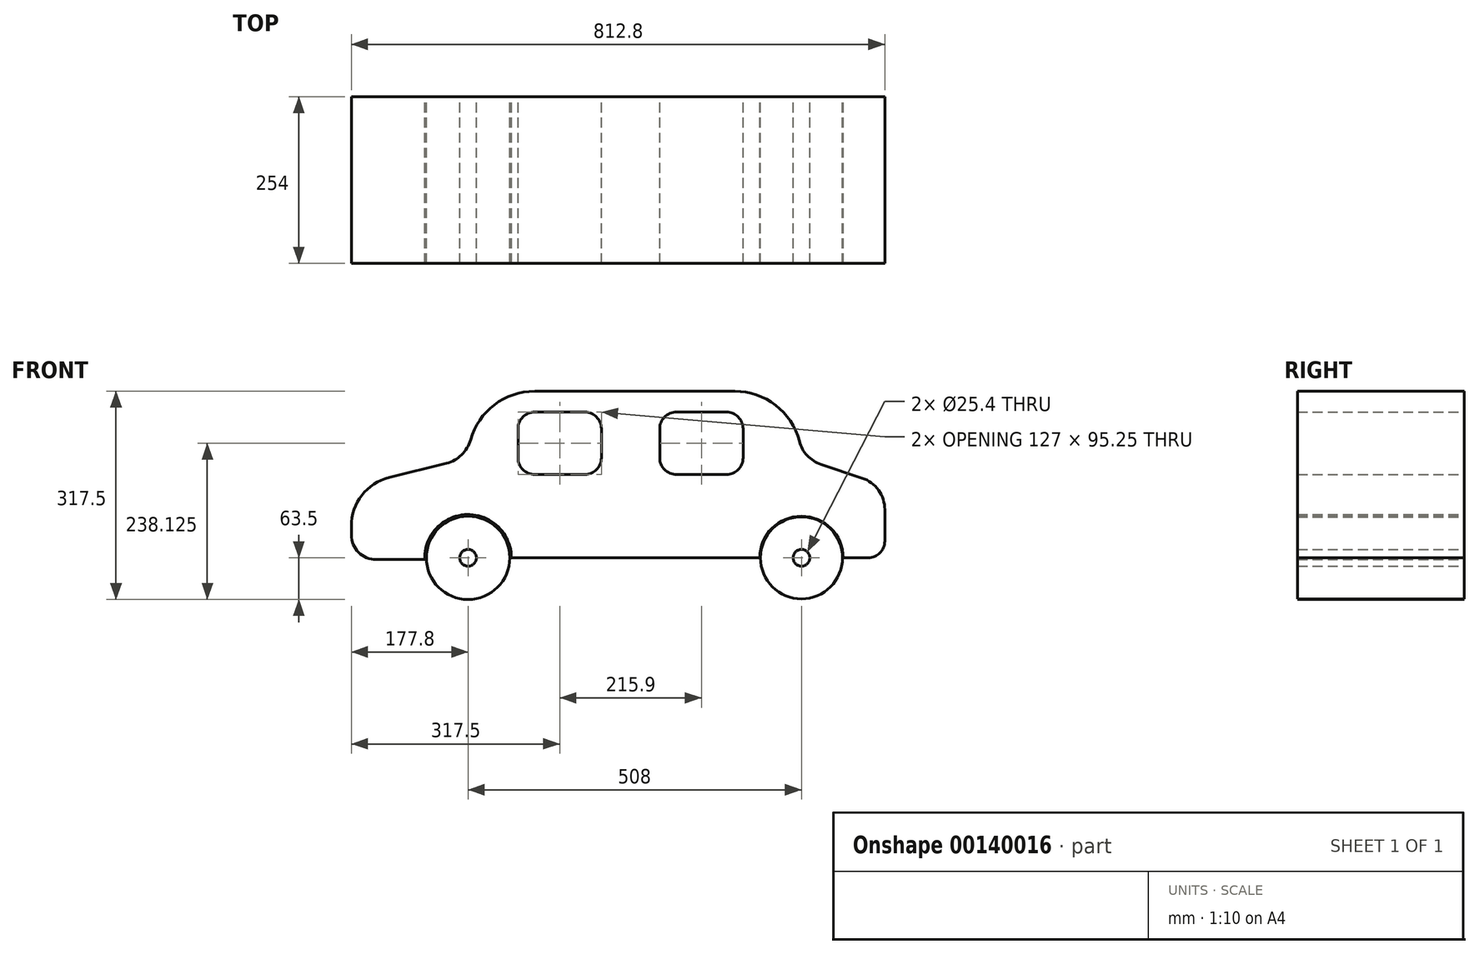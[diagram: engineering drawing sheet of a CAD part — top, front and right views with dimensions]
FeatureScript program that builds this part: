
annotation { "Feature Type Name" : "Feature", "Feature Type Description" : "" }
export const myFeature = defineFeature(function(context is Context, id is Id, definition is map)
    precondition{}
    {
        {
            var Q0;
            Q0=qCreatedBy(makeId("Front.planeOp"),FACE);
            var sketch = newSketch(context, id + "F0", { "sketchPlane" : qUnion([Q0])});
            skLineSegment(sketch, "E0.bottom", {"start": v(-152.4, 127) * mm, "end": v(152.4, 127) * mm});
            skLineSegment(sketch, "E0.left", {"start": v(-254, 25.4) * mm, "end": v(-254, 25.4) * mm});
            skLineSegment(sketch, "E0.right", {"start": v(254, 25.4) * mm, "end": v(254, 25.4) * mm});
            skPoint(sketch, "E0.middle", {"position": v(0, 0) * mm});
            skLineSegment(sketch, "E1.top", {"start": v(316.52, -127) * mm, "end": v(355.6, -127) * mm});
            skLineSegment(sketch, "E1.left", {"start": v(254, -127) * mm, "end": v(254, -127) * mm});
            skLineSegment(sketch, "E1.right", {"start": v(381, -53.55) * mm, "end": v(381, -101.6) * mm});
            skLineSegment(sketch, "E2.top", {"start": v(-319.98, -129.78) * mm, "end": v(-393.7, -129.78) * mm});
            skLineSegment(sketch, "E2.left", {"start": v(-254, -127) * mm, "end": v(-254, -129.78) * mm});
            skLineSegment(sketch, "E2.right", {"start": v(-431.8, -78.55) * mm, "end": v(-431.8, -91.68) * mm});
            skPoint(sketch, "E3.visualSharp", {"position": v(-254, 127) * mm});
            skPoint(sketch, "E4.visualSharp", {"position": v(254, 127) * mm});
            skArc(sketch, "E4.filletArc", {"start": v(250.75, 50.9) * mm, "mid": v(214.58, 105.75) * mm, "end": v(152.4, 127) * mm});
            skPoint(sketch, "E5.visualSharp", {"position": v(254, 25.4) * mm});
            skPoint(sketch, "E6.visualSharp", {"position": v(254, 0) * mm});
            skPoint(sketch, "E7.visualSharp", {"position": v(381, 0) * mm});
            skArc(sketch, "E7.filletArc", {"start": v(381, -53.55) * mm, "mid": v(371.41, -23.84) * mm, "end": v(346.26, -5.35) * mm});
            skPoint(sketch, "E8.visualSharp", {"position": v(-254, 0) * mm});
            skPoint(sketch, "E9.visualSharp", {"position": v(-431.8, 0) * mm});
            skArc(sketch, "E9.filletArc", {"start": v(-374.08, -4.62) * mm, "mid": v(-415.66, -31.65) * mm, "end": v(-431.8, -78.55) * mm});
            skPoint(sketch, "E10.visualSharp", {"position": v(-431.8, -129.78) * mm});
            skArc(sketch, "E10.filletArc", {"start": v(-431.8, -91.68) * mm, "mid": v(-420.64, -118.62) * mm, "end": v(-393.7, -129.78) * mm});
            skPoint(sketch, "E11.visualSharp", {"position": v(381, -127) * mm});
            skArc(sketch, "E11.filletArc", {"start": v(355.6, -127) * mm, "mid": v(373.56, -119.56) * mm, "end": v(381, -101.6) * mm});
            skLineSegment(sketch, "E12.bottom", {"start": v(-152.4, 95.25) * mm, "end": v(-76.2, 95.25) * mm});
            skLineSegment(sketch, "E12.top", {"start": v(-152.4, 0) * mm, "end": v(-76.2, 0) * mm});
            skLineSegment(sketch, "E12.left", {"start": v(-177.8, 69.85) * mm, "end": v(-177.8, 25.4) * mm});
            skLineSegment(sketch, "E12.right", {"start": v(-50.8, 69.85) * mm, "end": v(-50.8, 25.4) * mm});
            skPoint(sketch, "E13.visualSharp", {"position": v(-177.8, 95.25) * mm});
            skArc(sketch, "E13.filletArc", {"start": v(-152.4, 95.25) * mm, "mid": v(-170.36, 87.81) * mm, "end": v(-177.8, 69.85) * mm});
            skPoint(sketch, "E14.visualSharp", {"position": v(-50.8, 95.25) * mm});
            skArc(sketch, "E14.filletArc", {"start": v(-50.8, 69.85) * mm, "mid": v(-58.24, 87.81) * mm, "end": v(-76.2, 95.25) * mm});
            skPoint(sketch, "E15.visualSharp", {"position": v(-50.8, 0) * mm});
            skArc(sketch, "E15.filletArc", {"start": v(-76.2, 0) * mm, "mid": v(-58.24, 7.44) * mm, "end": v(-50.8, 25.4) * mm});
            skPoint(sketch, "E16.visualSharp", {"position": v(-177.8, 0) * mm});
            skArc(sketch, "E16.filletArc", {"start": v(-177.8, 25.4) * mm, "mid": v(-170.36, 7.44) * mm, "end": v(-152.4, 0) * mm});
            skCircle(sketch, "E17", {"center": v(-254, -127) * mm, "radius": 63.5 * mm});
            skArc(sketch, "E18", {"start": v(317.5, -127) * mm, "mid": v(254, -63.5) * mm, "end": v(190.5, -127) * mm});
            skArc(sketch, "E19.0", {"start": v(-187.96, -127) * mm, "mid": v(-255.4, -60.97) * mm, "end": v(-319.98, -129.78) * mm});
            skCircle(sketch, "E20.0", {"center": v(254, -127) * mm, "radius": 62.52 * mm});
            skLineSegment(sketch, "E21.trimOffspring", {"start": v(-187.96, -127) * mm, "end": v(190.5, -127) * mm});
            skLineSegment(sketch, "E22.MirrorCS", {"start": v(-147, -307.73) * mm, "end": v(-175.77, -334.2) * mm});
            skLineSegment(sketch, "E23.1.0.0", {"start": v(38.1, 69.85) * mm, "end": v(38.1, 25.4) * mm});
            skPoint(sketch, "E23.1.0.1", {"position": v(165.1, 95.25) * mm});
            skPoint(sketch, "E23.1.0.2", {"position": v(165.1, 0) * mm});
            skLineSegment(sketch, "E23.1.0.3", {"start": v(63.5, 0) * mm, "end": v(139.7, 0) * mm});
            skLineSegment(sketch, "E23.1.0.4", {"start": v(63.5, 95.25) * mm, "end": v(139.7, 95.25) * mm});
            skLineSegment(sketch, "E23.1.0.5", {"start": v(165.1, 69.85) * mm, "end": v(165.1, 25.4) * mm});
            skArc(sketch, "E23.1.0.6", {"start": v(38.1, 25.4) * mm, "mid": v(45.54, 7.44) * mm, "end": v(63.5, 0) * mm});
            skArc(sketch, "E23.1.0.7", {"start": v(139.7, 0) * mm, "mid": v(157.66, 7.44) * mm, "end": v(165.1, 25.4) * mm});
            skPoint(sketch, "E23.1.0.8", {"position": v(38.1, 95.25) * mm});
            skArc(sketch, "E23.1.0.9", {"start": v(63.5, 95.25) * mm, "mid": v(45.54, 87.81) * mm, "end": v(38.1, 69.85) * mm});
            skArc(sketch, "E23.1.0.10", {"start": v(165.1, 69.85) * mm, "mid": v(157.66, 87.81) * mm, "end": v(139.7, 95.25) * mm});
            skPoint(sketch, "E23.1.0.11", {"position": v(38.1, 0) * mm});
            skLineSegment(sketch, "E23.direction1", {"start": v(-177.8, 0) * mm, "end": v(38.1, 0) * mm, "construction": true});
            skArc(sketch, "E24.filletArc", {"start": v(-152.4, 127) * mm, "mid": v(-213.8, 106.35) * mm, "end": v(-250.24, 52.78) * mm});
            skLineSegment(sketch, "E25", {"start": v(-374.08, -4.62) * mm, "end": v(-286.84, 17.19) * mm});
            skPoint(sketch, "E26.visualSharp", {"position": v(-254, 25.4) * mm});
            skArc(sketch, "E26.filletArc", {"start": v(-286.84, 17.19) * mm, "mid": v(-263.74, 30.05) * mm, "end": v(-250.24, 52.78) * mm});
            skLineSegment(sketch, "E27", {"start": v(283.86, 15.45) * mm, "end": v(346.26, -5.35) * mm});
            skArc(sketch, "E28.filletArc", {"start": v(250.75, 50.9) * mm, "mid": v(262.8, 28.96) * mm, "end": v(283.86, 15.45) * mm});
            skCircle(sketch, "E29", {"center": v(-254, -127) * mm, "radius": 12.7 * mm});
            skCircle(sketch, "E30", {"center": v(254, -127) * mm, "radius": 12.7 * mm});
            skSolve(sketch);
        }
        {
            var Q0;
            Q0=makeQuery(id+"F0.imprint","IMPRINT",FACE,{"disambiguationData":[TD([[makeQuery(id+"F0.imprint","IMPRINT",EDGE,{"derivedFrom":sQuery(id+"F0.wireOp",EDGE,"E0.bottom")}),-1.0]])]});
            var Q1;
            Q1=makeQuery(id+"F0.imprint","IMPRINT",FACE,{"disambiguationData":[TD([[makeQuery(id+"F0.imprint","IMPRINT",EDGE,{"derivedFrom":sQuery(id+"F0.wireOp",EDGE,"E17")}),1.0]])]});
            var Q2;
            Q2=makeQuery(id+"F0.imprint","IMPRINT",FACE,{"disambiguationData":[TD([[makeQuery(id+"F0.imprint","IMPRINT",EDGE,{"derivedFrom":sQuery(id+"F0.wireOp",EDGE,"E20.0")}),1.0]])]});
            extrude(context, id + "F1", {"entities" : qUnion([Q0, Q1, Q2]), "depth" : 254 * mm});
        }
    });
